# Revit family: Armario Linkeo con única puerta anchura 600
name_source: partatom
category: Equipement spécialisé
units: mm (PartAtom-declared; Revit-internal decimal feet)

## family parameters
Basée sur le plan de construction = Non
Cote de connecteur circulaire = Utiliser le diamètre
Couper avec des vides une fois chargée = Non
Numéro OmniClass = 23.85.05.17.11.14
Partagée = Oui
Point de calcul de pièce = Non
Titre OmniClass = Multimedia Broadcasting Equipment
Toujours verticalement = Oui
Type d'élément = Normal

## types (5) — shared parameters
Acabado del carril de perfil = Acodado
Anchura (mm) = 610 mm  [stored 2.00131 ft]
Clase de aplicación = EC002499
Clase de protección IK = IK08
Clase de protección IP = IP20
Color = gris
Con conexión a tierra = Oui
Con puerta frontal = Oui
Con techo en chapa = Oui
E-catalogo enlace = https://www.legrand.fr
Fabricant = Legrand
Función = Armario Linkeo2
Material = Acero
Material de la puerta frontal = vidrio
Modelo = Estructura fija
Modelo de anchura = 600 mm
Máxima capacidad de carga = 400
Numero RAL = 7016
Número de puertas = 1
Simbolo de la puerta = Simbolo de la puerta  Puerta 600mm
Sistema de cierre de la puerta frontal = Un punto
Tamaño modular = 19 pulgadas
Temperatura de almacenamiento = -25°C à 70°C
Temperatura operativa = -25°C à 70°C
Tipo de montaje = Frontal
Tipo de ventilación = Ninguna
Tratamiento de superficie = Recubrimiento con polvo
Ubicación del rack = 93 mm  [stored 0.305118 ft]
zero-valued in all types: Elévation par défaut

## per-type parameters (varying)
| type | Altura | Altura útil (mm) | Anchura útil (mm) | Distancia de la apertura 1 | EAN | Módulos de altura | Número de pieza Legrand | Profundidad | Profundidad del modelo (mm) | Tipo de patas niveladoras | Tipo de perfiles horizontales | Tipo de perfiles verticales |
| Armario Linkeo2 24U 600x600 | 1226 mm  [stored 4.02231 ft] | 1081 mm  [stored 3.54659 ft] | 490 mm  [stored 1.60761 ft] | 57 mm  [stored 0.187008 ft] | 3414971001503 | 24 | 646750 | 630 mm  [stored 2.06693 ft] | 600 mm | Patas niveladoras  600X600 | Perfiles horizontales para armarios Linkeo  24U profundidad 600 | Perfiles verticales para armarios Linkeo  24U |
| Armario Linkeo2 42U 600x800 | 2026 mm | 1881 mm  [stored 6.17126 ft] | 690 mm  [stored 2.26378 ft] | 257 mm  [stored 0.843176 ft] | 3414971001558 | 42 | 646761 | 830 mm  [stored 2.7231 ft] | 800 mm  [stored 2.62467 ft] | Patas niveladoras  600X800 | Perfiles horizontales para armarios Linkeo  42U profundidad 800 | Perfiles verticales para armarios Linkeo  42U |
| Armario Linkeo2 33U 600x600 | 1626 mm | 1481 mm  [stored 4.85892 ft] | 490 mm  [stored 1.60761 ft] | 57 mm  [stored 0.187008 ft] | 3414971001527 | 33 | 646755 | 630 mm  [stored 2.06693 ft] | 600 mm | Patas niveladoras  600X600 | Perfiles horizontales para armarios Linkeo  33U profundidad 600 | Perfiles verticales para armarios Linkeo  33U |
| Armario Linkeo2 42U 600x600 | 2026 mm | 1881 mm  [stored 6.17126 ft] | 490 mm  [stored 1.60761 ft] | 57 mm  [stored 0.187008 ft] | 3414971001541 | 42 | 646760 | 630 mm  [stored 2.06693 ft] | 600 mm | Patas niveladoras  600X600 | Perfiles horizontales para armarios Linkeo  42U profundidad 600 | Perfiles verticales para armarios Linkeo  42U |
| Armario Linkeo2 42U 600x1000 | 2026 mm | 1881 mm  [stored 6.17126 ft] | 890 mm  [stored 2.91995 ft] | 457 mm  [stored 1.49934 ft] | 3414971001565 | 42 | 646762 | 1030 mm  [stored 3.37927 ft] | 1000 mm  [stored 3.28084 ft] | Patas niveladoras  600X1000 | Perfiles horizontales para armarios Linkeo  42U profundidad 1000 | Perfiles verticales para armarios Linkeo  42U |

note: column(s) folded — value = type name in every type: Formulación BIM

note: [stored X ft] marks values corroborated as IEEE doubles in the binary element streams (Revit-internal decimal feet)
